# Revit family: CCTYP06
name_source: partatom
category: Furniture
units: mm (PartAtom-declared; Revit-internal decimal feet)

## family parameters
Always vertical = Yes
Cut with Voids When Loaded = No
OmniClass Number = 23.40.20.00
OmniClass Title = General Furniture and Specialties
Render Appearance Source = Family Geometry
Room Calculation Point = No
Shared = No
Work Plane-Based = No

## types (1)
- CCTYP06
    Cost = 8627 $
    Default Elevation = 0 mm  [stored 0 ft]
    Description = 3 x Paxton - Casters - Black Mesh Back - Black Seat Fabric, 1 x Wall Mounted Overhead w/Cabinet Doors-16Hx42Wx14D, 1 x Wall Mounted Overhead w/Cabinet Doors-16Hx48Wx14D, 1 x Tbl, Rnd, 2mm, 42dx29h, Stlx36, Gld, 1 x CBX Wall Mounted L Shelf Vertical 16Hx48Wx12D, 1 x CBX Wall Mounted L Shelf Vertical 45Hx42Wx12D
    Exported From CET Designer = Yes
    Manufacturer = AIS
    Model = 3430
    Show CCTYP06 = Yes
    VisibilityIndex = 0

note: [stored X ft] marks values corroborated as IEEE doubles in the binary element streams (Revit-internal decimal feet)

## geometry (parser evidence)
native form markers: Sweep x3
no freeform markers — native parametric forms only
